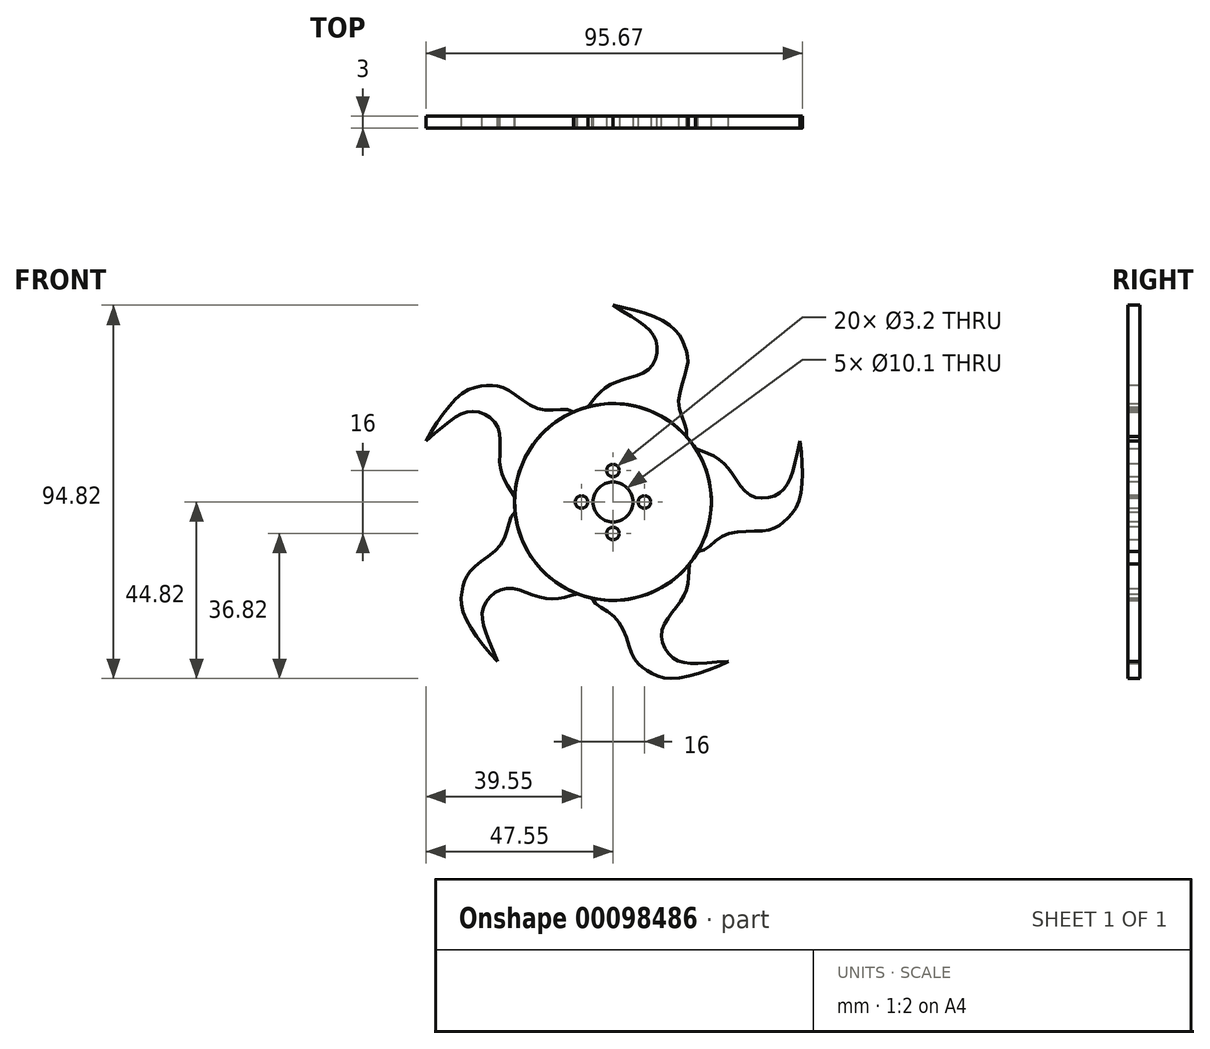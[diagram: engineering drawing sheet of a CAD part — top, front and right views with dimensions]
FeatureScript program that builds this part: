
annotation { "Feature Type Name" : "Feature", "Feature Type Description" : "" }
export const myFeature = defineFeature(function(context is Context, id is Id, definition is map)
    precondition{}
    {
        {
            var Q0;
            Q0=qCreatedBy(makeId("Front.planeOp"),FACE);
            var sketch = newSketch(context, id + "F0", { "sketchPlane" : qUnion([Q0])});
            skCircle(sketch, "E0", {"center": v(0, 0) * mm, "radius": 50 * mm, "construction": true});
            skCircle(sketch, "E1", {"center": v(0, 0) * mm, "radius": 25 * mm});
            skFitSpline(sketch, "E2", {"points": [v(0, 50) * mm, v(14.6, 44.79) * mm, v(18.26, 39.59) * mm, v(18.9, 34.67) * mm, v(16.74, 24.4) * mm, v(18.65, 16.65) * mm], "startDerivative": vector(61.52, -11.38) * mm, "endDerivative": vector(-10.6, -36.77) * mm});
            skFitSpline(sketch, "E3", {"points": [v(0, 50) * mm, v(10.8, 41.27) * mm, v(9.2, 33.82) * mm, v(0, 30.17) * mm, v(-6.4, 24.17) * mm], "startDerivative": vector(61.6, -38.88) * mm, "endDerivative": vector(-24.26, -32.03) * mm});
            skSolve(sketch);
        }
        {
            var Q0;
            Q0=makeQuery(id+"F0.imprint","IMPRINT",FACE,{"disambiguationData":[TD([[makeQuery(id+"F0.imprint","IMPRINT",EDGE,{"derivedFrom":sQuery(id+"F0.wireOp",EDGE,"E2")}),-1.0]])]});
            var Q1;
            {var subQ0=sQuery(id+"F0.wireOp",EDGE,"E1");var subQ1=makeQuery(id+"F0.imprint","INTERSECT",VERTEX,{"derivedFrom":[subQ0,sQuery(id+"F0.wireOp",EDGE,"E2")]});Q1=makeQuery(id+"F0.imprint","IMPRINT",FACE,{"disambiguationData":[TD([[makeQuery(id+"F0.imprint","IMPRINT",EDGE,{"disambiguationData":[TD([[subQ1,-1.0]])],"derivedFrom":subQ0}),1.0]])]});}
            extrude(context, id + "F1", {"entities" : qUnion([Q0, Q1]), "depth" : 3 * mm});
        }
        {
            var Q0;
            Q0=qCreatedBy(makeId("Right.planeOp"),FACE);
            var sketch = newSketch(context, id + "F2", { "sketchPlane" : qUnion([Q0])});
            skLineSegment(sketch, "E4", {"start": v(-18.7, 0) * mm, "end": v(27.7, 0) * mm, "construction": true});
            skSolve(sketch);
        }
        {
            var Q0;
            Q0=makeQuery(id+"F1.opExtrude","SWEPT_BODY",BODY,{"disambiguationData":[OSD([sQuery(id+"F0.wireOp",EDGE,"E2"),sQuery(id+"F0.wireOp",EDGE,"E3"),sQuery(id+"F0.wireOp",EDGE,"JvflZ2Xm-OZbW-fdge-9bIT-jv6nQqX975Xf")])]});
            var Q1;
            Q1=sQuery(id+"F2.wireOp",EDGE,"E4");
            circularPattern(context, id + "F3", {"entities" : qUnion([Q0]), "axis" : qUnion([Q1]), "angle" : 360 * degree, "instanceCount" : 5, "equalSpace" : true});
        }
        {
            var Q0;
            Q0=makeQuery(id+"F3.opPattern","COPY",FACE,{"derivedFrom":makeQuery(id+"F1.opExtrude","CAP_FACE",FACE,{"disambiguationData":[OSD([sQuery(id+"F0.wireOp",EDGE,"E1"),sQuery(id+"F0.wireOp",EDGE,"E2"),sQuery(id+"F0.wireOp",EDGE,"E3")])],"isStart":false}),"instanceName":"3"});
            var sketch = newSketch(context, id + "F4", { "sketchPlane" : qUnion([Q0])});
            skCircle(sketch, "E5", {"center": v(0, 0) * mm, "radius": 8 * mm, "construction": true});
            skCircle(sketch, "E6", {"center": v(0, 8) * mm, "radius": 1.6 * mm});
            skCircle(sketch, "E7.1.0", {"center": v(-8, 0) * mm, "radius": 1.6 * mm});
            skCircle(sketch, "E7.2.0", {"center": v(0, -8) * mm, "radius": 1.6 * mm});
            skCircle(sketch, "E7.3.0", {"center": v(8, 0) * mm, "radius": 1.6 * mm});
            skCircle(sketch, "E8", {"center": v(0, 0) * mm, "radius": 5.05 * mm});
            skSolve(sketch);
        }
        {
            var Q0;
            Q0 = qSketchRegion(id + "F4", true);
            extrude(context, id + "F5", {"entities" : qUnion([Q0]), "operationType" : NewBodyOperationType.REMOVE, "endBound" : BoundingType.UP_TO_NEXT, "oppositeDirection" : true, "depth" : 25 * mm});
        }
    });
